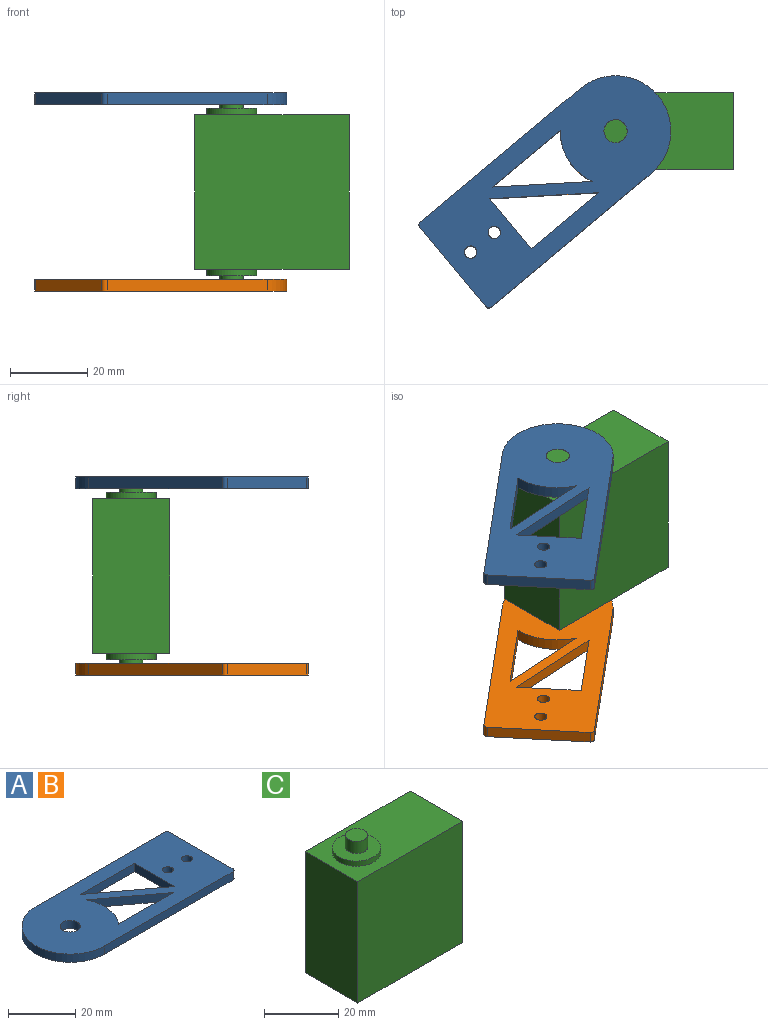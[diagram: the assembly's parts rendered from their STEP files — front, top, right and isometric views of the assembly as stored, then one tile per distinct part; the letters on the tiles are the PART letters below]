
ASSEMBLY  parts=3 mates=5
PART A: 17 faces, bbox 69.4x28.7x3 mm
  f0: plane 54x3mm, normal (0,1,0), area 162mm2, adj f1,f13,f14,f16
  f1: cylinder r=14.37mm len=28.74mm, axis (0,0,-1), area 135.4mm2, adj f0,f2,f13,f14
  f2: plane 54x3mm, normal (0,-1,0), area 162mm2, adj f1,f13,f14,f15
  f3: cylinder r=14.37mm len=15.55mm, axis (0,0,-1), area 49.8mm2, adj f4,f7,f13,f14
  f4: plane 20.9x15.55mm, normal (-0.6,-0.8,0), area 78.2mm2, adj f3,f7,f13,f14
  f5: plane 22.72x16.9mm, normal (0.6,0.8,0), area 85mm2, adj f6,f8,f13,f14
  f6: plane 22.72x3mm, normal (0,-1,0), area 68.2mm2, adj f5,f8,f13,f14
  f7: plane 23x3mm, normal (0,1,0), area 69mm2, adj f3,f4,f13,f14
  f8: plane 16.9x3mm, normal (-1,0,0), area 50.7mm2, adj f5,f6,f13,f14
  f9: cylinder r=3mm len=6mm, axis (0,0,-1), area 56.5mm2, adj f13,f14
  f10: cylinder r=1.6mm len=3.2mm, axis (0,0,-1), area 30.2mm2, adj f13,f14
  f11: cylinder r=1.6mm len=3.2mm, axis (0,0,-1), area 30.2mm2, adj f13,f14
  f12: plane 26.74x3mm, normal (1,0,0), area 80.2mm2, adj f13,f14,f15,f16
  f13: plane 69.37x28.74mm, normal (0,0,1), area 1514.2mm2, adj f0,f1,f2,f3,f4,f5,f6,f7
  f14: plane 69.37x28.74mm, normal (0,0,-1), area 1514.2mm2, adj f0,f1,f2,f3,f4,f5,f6,f7
  f15: cylinder r=1mm len=3mm, axis (0,0,-1), area 4.7mm2, adj f2,f12,f13,f14
  f16: cylinder r=1mm len=3mm, axis (0,0,1), area 4.7mm2, adj f0,f12,f13,f14
PART B: same geometry as A
PART C: 14 faces, bbox 40x20x51.4 mm
  f0: plane 40x40mm, normal (0,1,0), area 1600mm2, adj f1,f3,f4,f5
  f1: plane 40x20mm, normal (-1,0,0), area 800mm2, adj f0,f2,f4,f5
  f2: plane 40x40mm, normal (0,-1,0), area 1600mm2, adj f1,f3,f4,f5
  f3: plane 40x20mm, normal (1,0,0), area 800mm2, adj f0,f2,f4,f5
  f4: plane 40x20mm, normal (0,0,1), area 667.3mm2, adj f0,f1,f2,f3,f6
  f5: plane 40x20mm, normal (0,0,-1), area 667.3mm2, adj f0,f1,f2,f3,f10
  f6: cylinder r=6.5mm len=13mm, axis (0,0,-1), area 69.4mm2, adj f4,f7
  f7: plane 13x13mm, normal (0,0,1), area 104.5mm2, adj f6,f8
  f8: cylinder r=3mm len=6mm, axis (0,0,-1), area 75.4mm2, adj f7,f9
  f9: plane 6x6mm, normal (0,0,1), area 28.3mm2, adj f8
  f10: cylinder r=6.5mm len=13mm, axis (0,0,1), area 69.4mm2, adj f5,f11
  f11: plane 13x13mm, normal (0,0,-1), area 104.5mm2, adj f10,f12
  f12: cylinder r=3mm len=6mm, axis (0,0,1), area 75.4mm2, adj f11,f13
  f13: plane 6x6mm, normal (0,0,-1), area 28.3mm2, adj f12
PLACE A rot(axis=(0,0,-1),140.1deg) t=(49.23,51.91,-12.47)mm
PLACE B rot(axis=(0,0,-1),140.1deg) t=(49.23,51.91,-60.87)mm
PLACE C t=(31.66,16.46,-55.17)mm
MATE planar C.f6 <-> B.f14  axis (0,0,-1) through (41.16,26.46,-60.87)mm
MATE planar C.f6 <-> A.f13  axis (0,0,1) through (41.16,26.46,-9.47)mm
MATE planar A.f12 <-> B.f12  axis (-0.77,-0.64,0) through (-1.06,-8.79,-10.97)mm
MATE cylindrical A.f1 <-> C.f6  axis (0,0,1) through (41.16,26.46,-9.47)mm
MATE cylindrical C.f6 <-> B.f1  axis (0,0,-1) through (41.16,26.46,-60.87)mm
